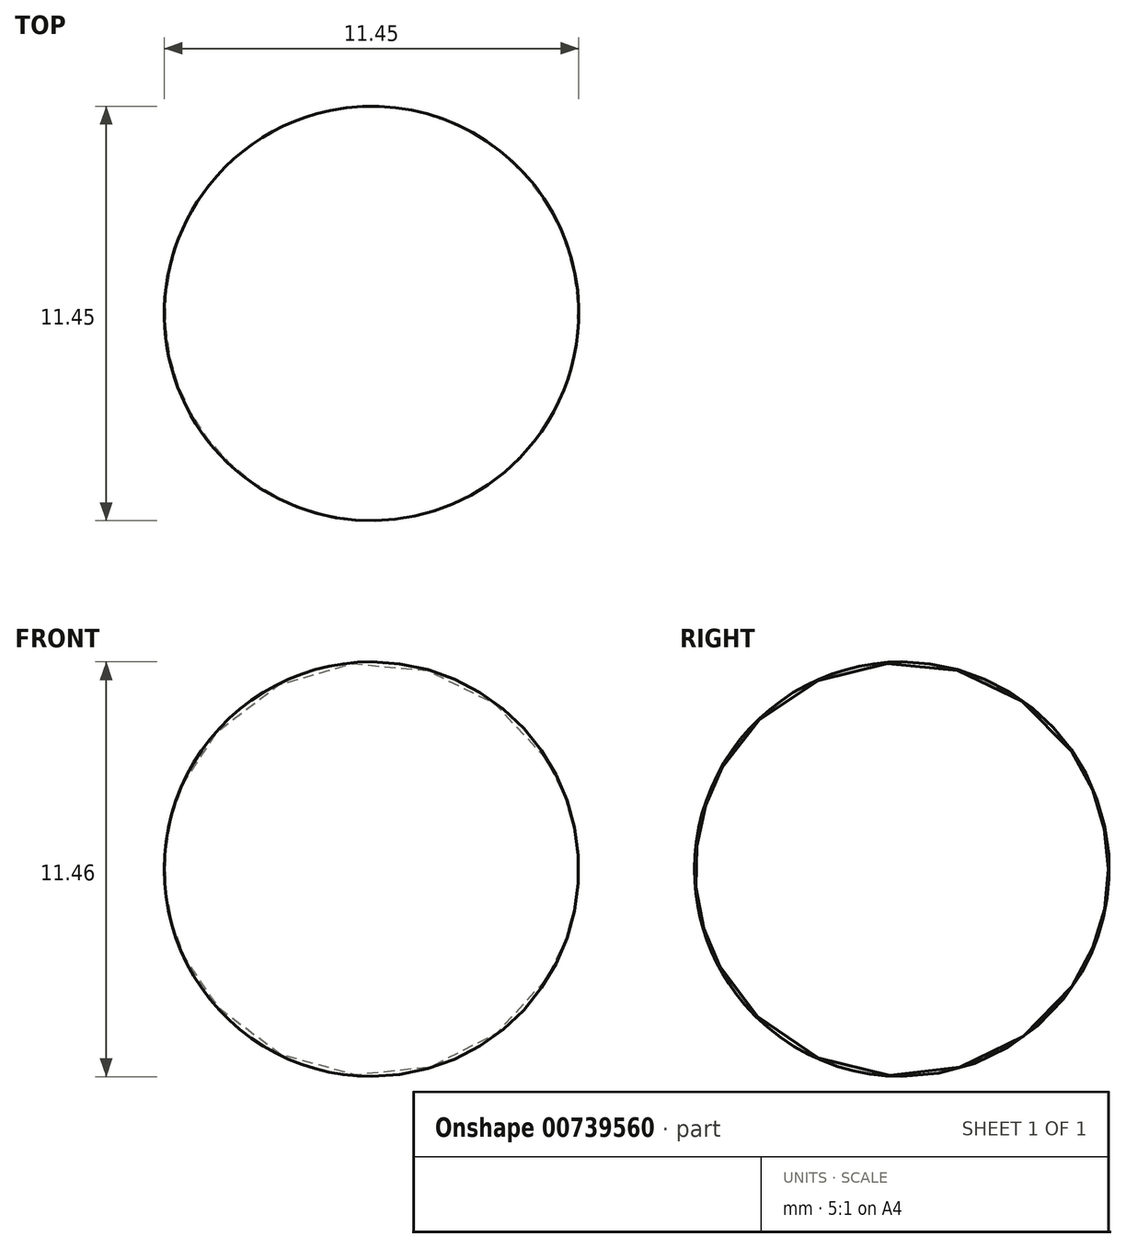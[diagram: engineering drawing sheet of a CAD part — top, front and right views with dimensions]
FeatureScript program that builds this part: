
annotation { "Feature Type Name" : "Feature", "Feature Type Description" : "" }
export const myFeature = defineFeature(function(context is Context, id is Id, definition is map)
    precondition{}
    {
        {
            var Q0;
            Q0=qCreatedBy(makeId("Top.planeOp"),FACE);
            var sketch = newSketch(context, id + "F0", { "sketchPlane" : qUnion([Q0])});
            skArc(sketch, "E0", {"start": v(-34.5, 50.74) * mm, "mid": v(-33.57, 42.7) * mm, "end": v(-25.53, 43.65) * mm});
            skLineSegment(sketch, "E1", {"start": v(-34.5, 50.74) * mm, "end": v(-25.53, 43.65) * mm});
            skSolve(sketch);
        }
        {
            var Q0;
            Q0=makeQuery(id+"F0.imprint","IMPRINT",FACE,{"disambiguationData":[TD([[makeQuery(id+"F0.imprint","IMPRINT",EDGE,{"derivedFrom":sQuery(id+"F0.wireOp",EDGE,"E0")}),1.0]])]});
            var Q1;
            Q1=sQuery(id+"F0.wireOp",EDGE,"E1");
            revolve(context, id + "F1", {"surfaceOperationType" : NewSurfaceOperationType.NEW, "entities" : qUnion([Q0]), "axis" : qUnion([Q1]), "revolveType" : RevolveType.FULL});
        }
    });
